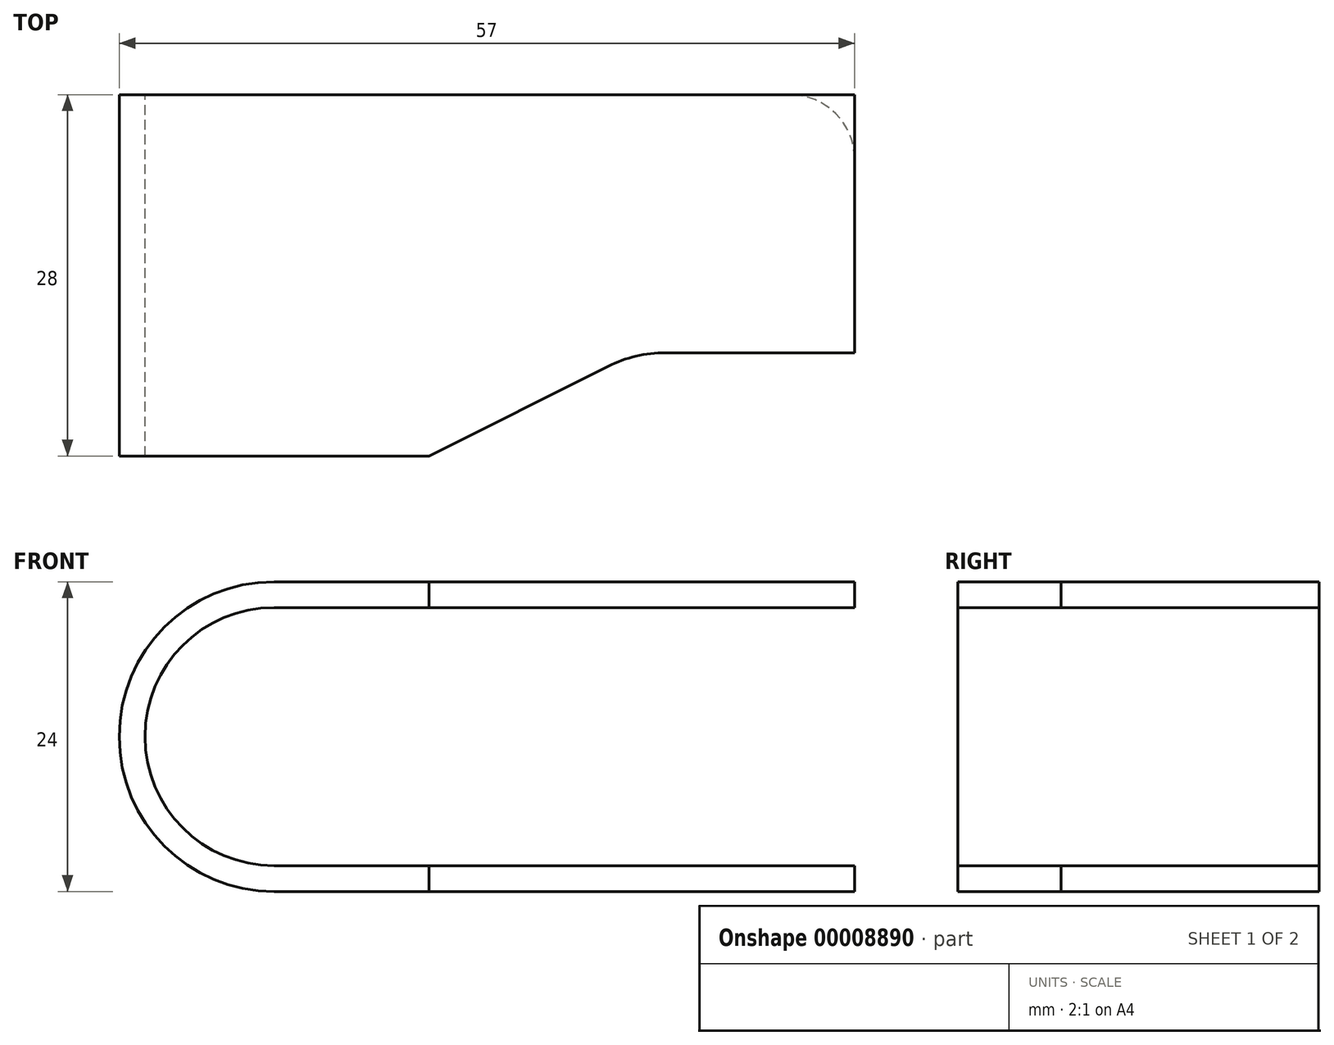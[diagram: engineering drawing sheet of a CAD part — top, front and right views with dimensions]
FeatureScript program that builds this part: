
annotation { "Feature Type Name" : "Feature", "Feature Type Description" : "" }
export const myFeature = defineFeature(function(context is Context, id is Id, definition is map)
    precondition{}
    {
        {
            var Q0;
            Q0=qCreatedBy(makeId("Front.planeOp"),FACE);
            var sketch = newSketch(context, id + "F0", { "sketchPlane" : qUnion([Q0])});
            skLineSegment(sketch, "E0.right", {"start": v(0, 1.5) * mm, "end": v(0, 21.5) * mm});
            skLineSegment(sketch, "E1.bottom", {"start": v(-45, -2) * mm, "end": v(0, -2) * mm});
            skLineSegment(sketch, "E1.top", {"start": v(-45, 22) * mm, "end": v(0, 22) * mm});
            skLineSegment(sketch, "E1.left", {"start": v(-45, -2) * mm, "end": v(-45, 22) * mm});
            skLineSegment(sketch, "E1.right", {"start": v(0, -2) * mm, "end": v(0, 22) * mm});
            skArc(sketch, "E2", {"start": v(-45, 22) * mm, "mid": v(-57, 10) * mm, "end": v(-45, -2) * mm});
            skCircle(sketch, "E3", {"center": v(-45, 10) * mm, "radius": 10 * mm});
            skLineSegment(sketch, "E4", {"start": v(0, 0) * mm, "end": v(-45, 0) * mm});
            skLineSegment(sketch, "E5", {"start": v(0, 20) * mm, "end": v(-45, 20) * mm});
            skSolve(sketch);
        }
        {
            var Q0;
            {var subQ4=sQuery(id+"F0.wireOp",EDGE,"E2");Q0=makeQuery(id+"F0.imprint","IMPRINT",FACE,{"disambiguationData":[TD([[makeQuery(id+"F0.imprint","IMPRINT",EDGE,{"derivedFrom":subQ4}),1.0]])]});}
            var Q1;
            {var subQ4=sQuery(id+"F0.wireOp",EDGE,"E0.bottom");Q1=makeQuery(id+"F0.imprint","IMPRINT",FACE,{"disambiguationData":[TD([[makeQuery(id+"F0.imprint","IMPRINT",EDGE,{"derivedFrom":subQ4}),-1.0]])]});}
            var Q2;
            {var subQ3=sQuery(id+"F0.wireOp",EDGE,"E0.top");Q2=makeQuery(id+"F0.imprint","IMPRINT",FACE,{"disambiguationData":[TD([[makeQuery(id+"F0.imprint","IMPRINT",EDGE,{"derivedFrom":subQ3}),1.0]])]});}
            var Q3;
            {var subQ5=sQuery(id+"F0.wireOp",EDGE,"E1.bottom");Q3=makeQuery(id+"F0.imprint","IMPRINT",FACE,{"disambiguationData":[TD([[makeQuery(id+"F0.imprint","IMPRINT",EDGE,{"derivedFrom":subQ5}),1.0]])]});}
            var Q4;
            {var subQ5=sQuery(id+"F0.wireOp",EDGE,"E1.top");Q4=makeQuery(id+"F0.imprint","IMPRINT",FACE,{"disambiguationData":[TD([[makeQuery(id+"F0.imprint","IMPRINT",EDGE,{"derivedFrom":subQ5}),-1.0]])]});}
            extrude(context, id + "F1", {"entities" : qUnion([Q0, Q1, Q2, Q3, Q4]), "depth" : 28 * mm});
        }
        {
            var Q0;
            Q0=makeQuery(id+"F1.opExtrude","SWEPT_FACE",FACE,{"disambiguationData":[OSD([sQuery(id+"F0.wireOp",EDGE,"E1.bottom")])]});
            var sketch = newSketch(context, id + "F2", { "sketchPlane" : qUnion([Q0])});
            skLineSegment(sketch, "E6", {"start": v(-33, 28) * mm, "end": v(-17, 20) * mm});
            skLineSegment(sketch, "E7", {"start": v(-17, 20) * mm, "end": v(0, 20) * mm});
            skLineSegment(sketch, "E8", {"start": v(-33, 28) * mm, "end": v(0, 28) * mm});
            skLineSegment(sketch, "E9", {"start": v(0, 28) * mm, "end": v(0, 20) * mm});
            skSolve(sketch);
        }
        {
            var Q0;
            Q0=makeQuery(id+"F2.imprint","IMPRINT",FACE,{"disambiguationData":[TD([[makeQuery(id+"F2.imprint","IMPRINT",EDGE,{"derivedFrom":sQuery(id+"F2.wireOp",EDGE,"E6")}),1.0]])]});
            extrude(context, id + "F3", {"entities" : qUnion([Q0]), "operationType" : NewBodyOperationType.REMOVE, "oppositeDirection" : true, "depth" : 50 * mm});
        }
        {
            var Q0;
            Q0=makeQuery(id+"F3.boolean.opBoolean","COPY",EDGE,{"disambiguationData":[OD(0.0)],"derivedFrom":makeQuery(id+"F3.opExtrude","SWEPT_EDGE",EDGE,{"disambiguationData":[OSD([sQuery(id+"F0.wireOp",EDGE,"E1.bottom"),sQuery(id+"F2.wireOp",EDGE,"E6"),sQuery(id+"F2.wireOp",EDGE,"E8")])]})});
            var Q1;
            Q1=makeQuery(id+"F3.boolean.opBoolean","COPY",EDGE,{"disambiguationData":[OD(1.0)],"derivedFrom":makeQuery(id+"F3.opExtrude","SWEPT_EDGE",EDGE,{"disambiguationData":[OSD([sQuery(id+"F0.wireOp",EDGE,"E1.bottom"),sQuery(id+"F2.wireOp",EDGE,"E6"),sQuery(id+"F2.wireOp",EDGE,"E8")])]})});
            var Q2;
            Q2=makeQuery(id+"F3.boolean.opBoolean","COPY",EDGE,{"disambiguationData":[OD(1.0)],"derivedFrom":makeQuery(id+"F3.opExtrude","SWEPT_EDGE",EDGE,{"disambiguationData":[OSD([sQuery(id+"F2.wireOp",EDGE,"E6"),sQuery(id+"F2.wireOp",EDGE,"E7")])]})});
            var Q3;
            Q3=makeQuery(id+"F3.boolean.opBoolean","COPY",EDGE,{"disambiguationData":[OD(0.0)],"derivedFrom":makeQuery(id+"F3.opExtrude","SWEPT_EDGE",EDGE,{"disambiguationData":[OSD([sQuery(id+"F2.wireOp",EDGE,"E6"),sQuery(id+"F2.wireOp",EDGE,"E7")])]})});
            fillet(context, id + "F4", {"entities" : qUnion([Q0, Q1, Q2, Q3]), "radius" : 10 * mm, "tangentPropagation" : true, "allowEdgeOverflow" : false});
        }
        {
            var Q0;
            Q0=makeQuery(id+"F3.boolean.opBoolean","COPY",EDGE,{"disambiguationData":[OD(0.0)],"derivedFrom":makeQuery(id+"F3.opExtrude","SWEPT_EDGE",EDGE,{"disambiguationData":[OSD([sQuery(id+"F0.wireOp",EDGE,"E1.bottom"),sQuery(id+"F0.wireOp",EDGE,"E1.right"),sQuery(id+"F2.wireOp",EDGE,"E7"),sQuery(id+"F2.wireOp",EDGE,"E9")])]})});
            var Q1;
            Q1=makeQuery(id+"F3.boolean.opBoolean","COPY",EDGE,{"disambiguationData":[OD(1.0)],"derivedFrom":makeQuery(id+"F3.opExtrude","SWEPT_EDGE",EDGE,{"disambiguationData":[OSD([sQuery(id+"F0.wireOp",EDGE,"E1.bottom"),sQuery(id+"F0.wireOp",EDGE,"E1.right"),sQuery(id+"F2.wireOp",EDGE,"E7"),sQuery(id+"F2.wireOp",EDGE,"E9")])]})});
            var Q2;
            {var subQ0=sQuery(id+"F0.wireOp",EDGE,"E1.right");Q2=makeQuery(id+"F1.opExtrude","CAP_EDGE",EDGE,{"disambiguationData":[OSD([subQ0]),TDD([makeQuery(id+"F0.imprint","IMPRINT",EDGE,{"disambiguationData":[TD([[makeQuery(id+"F0.imprint","INTERSECT",VERTEX,{"derivedFrom":[sQuery(id+"F0.wireOp",EDGE,"E1.top"),subQ0]}),1.0]])],"derivedFrom":subQ0})])],"isStart":true});}
            var Q3;
            {var subQ0=sQuery(id+"F0.wireOp",EDGE,"E1.right");Q3=makeQuery(id+"F1.opExtrude","CAP_EDGE",EDGE,{"disambiguationData":[OSD([subQ0]),TDD([makeQuery(id+"F0.imprint","IMPRINT",EDGE,{"disambiguationData":[TD([[makeQuery(id+"F0.imprint","INTERSECT",VERTEX,{"derivedFrom":[sQuery(id+"F0.wireOp",EDGE,"E1.bottom"),subQ0]}),-1.0]])],"derivedFrom":subQ0})])],"isStart":true});}
            fillet(context, id + "F5", {"entities" : qUnion([Q0, Q1, Q2, Q3]), "radius" : 5 * mm, "tangentPropagation" : true, "allowEdgeOverflow" : false});
        }
    });
